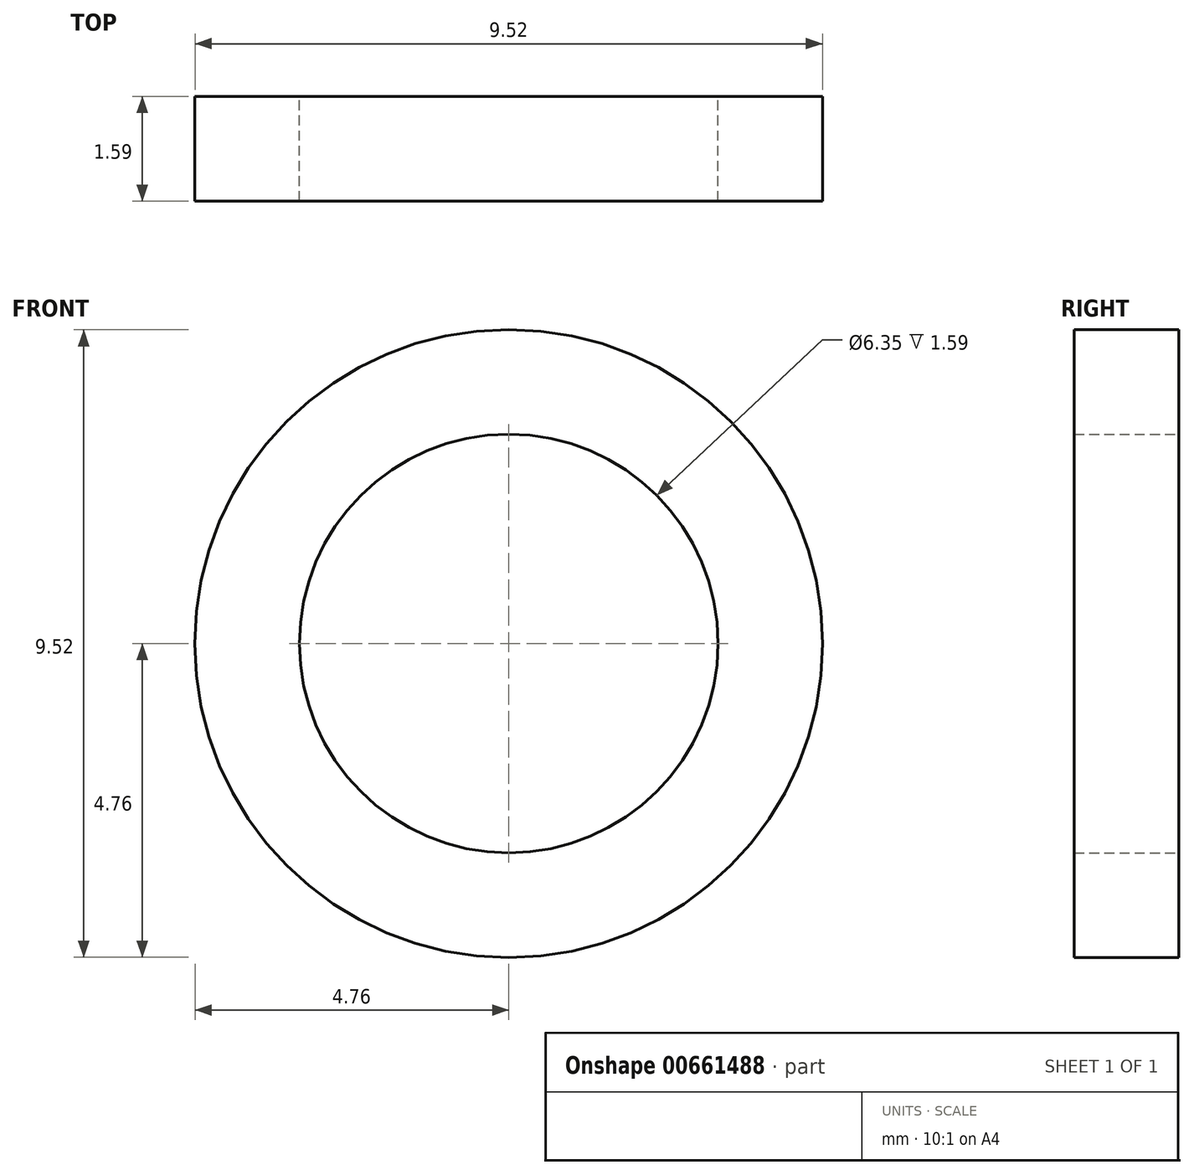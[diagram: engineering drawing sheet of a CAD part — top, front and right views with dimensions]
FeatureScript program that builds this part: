
annotation { "Feature Type Name" : "Feature", "Feature Type Description" : "" }
export const myFeature = defineFeature(function(context is Context, id is Id, definition is map)
    precondition{}
    {
        {
            var Q0;
            Q0=qCreatedBy(makeId("Front.planeOp"),FACE);
            var sketch = newSketch(context, id + "F0", { "sketchPlane" : qUnion([Q0])});
            skCircle(sketch, "E0", {"center": v(0, 0) * mm, "radius": 3.17 * mm});
            skCircle(sketch, "E1", {"center": v(0, 0) * mm, "radius": 4.76 * mm});
            skSolve(sketch);
        }
        {
            var Q0;
            Q0=makeQuery(id+"F0.imprint","IMPRINT",FACE,{"disambiguationData":[TD([[makeQuery(id+"F0.imprint","IMPRINT",EDGE,{"derivedFrom":sQuery(id+"F0.wireOp",EDGE,"E0")}),-1.0]])]});
            extrude(context, id + "F1", {"entities" : qUnion([Q0]), "depth" : 1.59 * mm, "offsetDistance" : 25 * mm});
        }
    });
